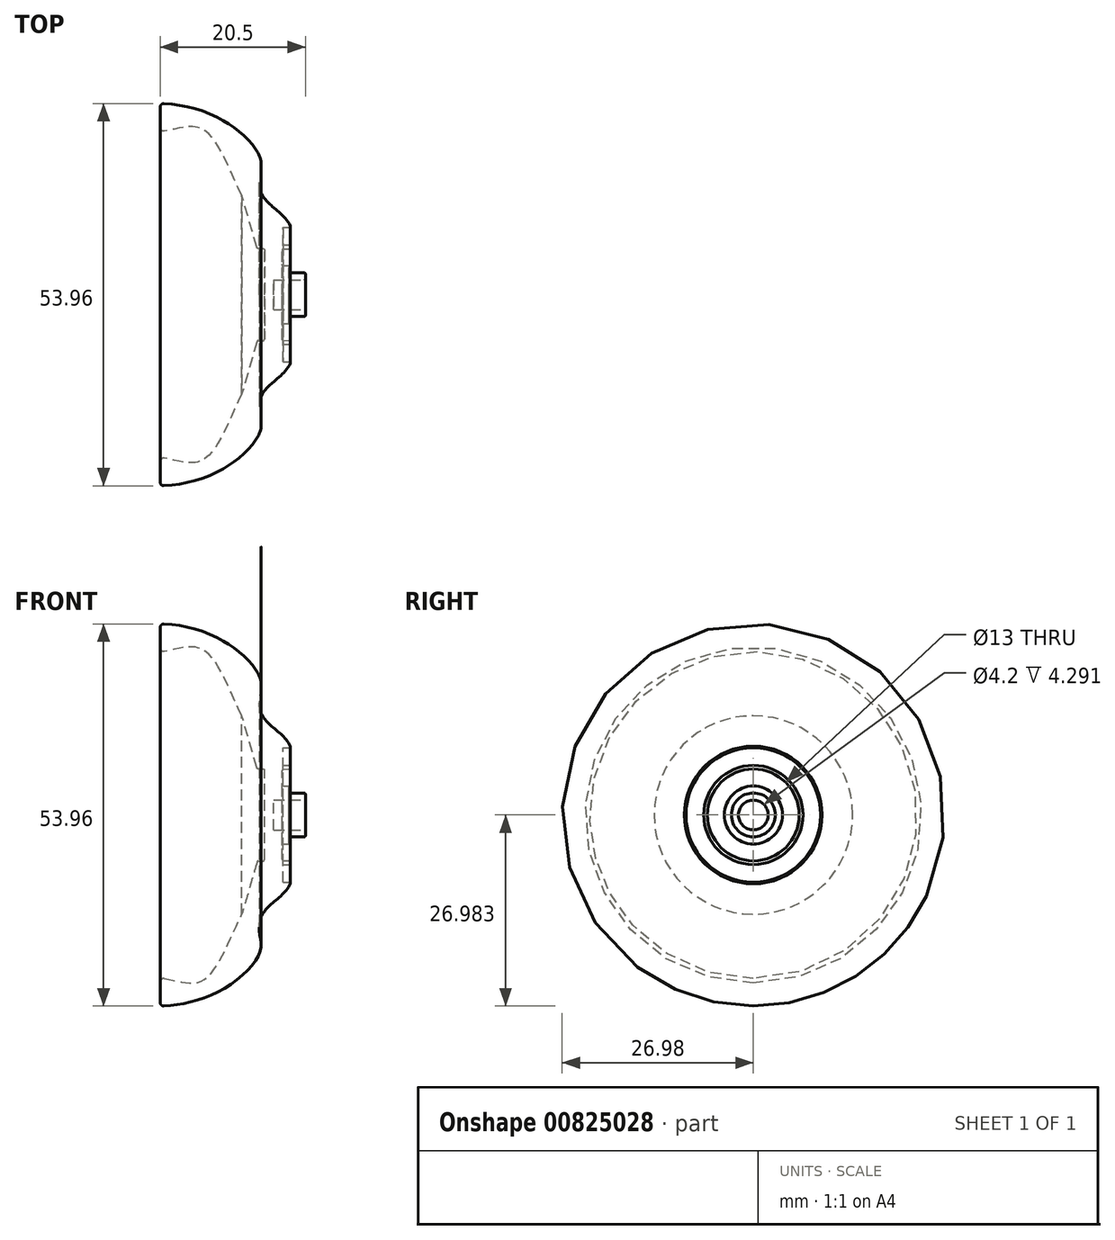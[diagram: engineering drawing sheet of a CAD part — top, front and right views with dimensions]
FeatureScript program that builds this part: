
annotation { "Feature Type Name" : "Feature", "Feature Type Description" : "" }
export const myFeature = defineFeature(function(context is Context, id is Id, definition is map)
    precondition{}
    {
        {
            var Q0;
            Q0=qCreatedBy(makeId("Front.planeOp"),FACE);
            var sketch = newSketch(context, id + "F0", { "sketchPlane" : qUnion([Q0])});
            skPoint(sketch, "E0", {"position": v(100.34, -4.5) * mm});
            skLineSegment(sketch, "E1", {"start": v(103.46, -7.12) * mm, "end": v(103.46, -6.52) * mm});
            skLineSegment(sketch, "E2", {"start": v(103.26, -6.32) * mm, "end": v(101.16, -6.32) * mm});
            skLineSegment(sketch, "E3", {"start": v(101.16, -6.32) * mm, "end": v(101.16, -5.52) * mm});
            skLineSegment(sketch, "E4", {"start": v(100.96, -5.32) * mm, "end": v(100.36, -5.32) * mm});
            skLineSegment(sketch, "E5", {"start": v(100.16, -5.12) * mm, "end": v(100.16, -3.16) * mm});
            skLineSegment(sketch, "E6", {"start": v(100.35, -2.96) * mm, "end": v(101.3, -2.94) * mm});
            skLineSegment(sketch, "E7", {"start": v(101.3, -2.94) * mm, "end": v(101.3, -2.42) * mm});
            skLineSegment(sketch, "E8", {"start": v(101.3, -2.42) * mm, "end": v(100.3, -2.42) * mm});
            skLineSegment(sketch, "E9", {"start": v(100.3, -2.42) * mm, "end": v(100.3, 0.08) * mm});
            skLineSegment(sketch, "E10", {"start": v(100.3, 0.08) * mm, "end": v(101.1, 0.08) * mm});
            skPoint(sketch, "E11.startSnap0", {"position": v(102.3, -6.32) * mm});
            skLineSegment(sketch, "E12", {"start": v(103.46, -9.42) * mm, "end": v(102.18, -9.42) * mm});
            skLineSegment(sketch, "E13", {"start": v(103.46, -9.42) * mm, "end": v(82.96, -9.42) * mm});
            skPoint(sketch, "E14.visualSharp", {"position": v(103.46, -7.32) * mm});
            skArc(sketch, "E14.filletArc", {"start": v(103.26, -7.32) * mm, "mid": v(103.4, -7.26) * mm, "end": v(103.46, -7.12) * mm});
            skPoint(sketch, "E15.visualSharp", {"position": v(103.46, -6.32) * mm});
            skArc(sketch, "E15.filletArc", {"start": v(103.46, -6.52) * mm, "mid": v(103.4, -6.38) * mm, "end": v(103.26, -6.32) * mm});
            skPoint(sketch, "E16.visualSharp", {"position": v(101.16, -5.32) * mm});
            skArc(sketch, "E16.filletArc", {"start": v(101.16, -5.52) * mm, "mid": v(101.1, -5.38) * mm, "end": v(100.96, -5.32) * mm});
            skPoint(sketch, "E17.visualSharp", {"position": v(100.16, -5.32) * mm});
            skArc(sketch, "E17.filletArc", {"start": v(100.16, -5.12) * mm, "mid": v(100.21, -5.26) * mm, "end": v(100.36, -5.32) * mm});
            skPoint(sketch, "E18.visualSharp", {"position": v(100.16, -2.97) * mm});
            skArc(sketch, "E18.filletArc", {"start": v(100.35, -2.96) * mm, "mid": v(100.21, -3.02) * mm, "end": v(100.16, -3.16) * mm});
            skPoint(sketch, "E19.visualSharp", {"position": v(101.3, 0.08) * mm});
            skArc(sketch, "E19.filletArc", {"start": v(101.1, 0.08) * mm, "mid": v(101.24, 0.15) * mm, "end": v(101.3, 0.3) * mm});
            skLineSegment(sketch, "E20", {"start": v(103.46, -9.42) * mm, "end": v(98.96, -9.42) * mm});
            skLineSegment(sketch, "E21", {"start": v(82.96, -9.42) * mm, "end": v(82.96, 17.58) * mm});
            skFitSpline(sketch, "E22", {"points": [v(82.96, 17.58) * mm, v(91.4, 15.4) * mm, v(97.04, 9.93) * mm, v(96.94, 6.98) * mm, v(97.74, 4.07) * mm, v(101.3, 0.3) * mm], "startDerivative": vector(30.11, -0.93) * mm, "endDerivative": vector(8.42, -22.03) * mm});
            skLineSegment(sketch, "E23", {"start": v(82.96, 17.06) * mm, "end": v(82.96, 14.16) * mm});
            skLineSegment(sketch, "E24", {"start": v(98.96, -9.42) * mm, "end": v(98.96, -7.32) * mm});
            skLineSegment(sketch, "E25", {"start": v(103.26, -7.32) * mm, "end": v(98.96, -7.32) * mm});
            skLineSegment(sketch, "E26", {"start": v(98.96, -9.42) * mm, "end": v(97.66, -9.42) * mm});
            skLineSegment(sketch, "E27", {"start": v(97.66, -9.42) * mm, "end": v(97.66, -3.12) * mm});
            skFitSpline(sketch, "E28", {"points": [v(82.96, 13.58) * mm, v(88.78, 14.01) * mm, v(94.49, 4.6) * mm], "startDerivative": vector(14.05, 1.46) * mm, "endDerivative": vector(10.13, -20.3) * mm});
            skArc(sketch, "E29.filletArc", {"start": v(83.5, 17.56) * mm, "mid": v(83.12, 17.42) * mm, "end": v(82.96, 17.06) * mm});
            skLineSegment(sketch, "E30", {"start": v(97.46, -2.92) * mm, "end": v(96.81, -2.92) * mm});
            skLineSegment(sketch, "E31", {"start": v(96.62, -2.77) * mm, "end": v(94.49, 4.6) * mm});
            skArc(sketch, "E32.filletArc", {"start": v(82.96, 14.16) * mm, "mid": v(83.14, 13.77) * mm, "end": v(83.55, 13.66) * mm});
            skPoint(sketch, "E33.visualSharp", {"position": v(97.66, -2.92) * mm});
            skArc(sketch, "E33.filletArc", {"start": v(97.66, -3.12) * mm, "mid": v(97.6, -2.98) * mm, "end": v(97.46, -2.92) * mm});
            skPoint(sketch, "E34.visualSharp", {"position": v(96.66, -2.92) * mm});
            skArc(sketch, "E34.filletArc", {"start": v(96.62, -2.77) * mm, "mid": v(96.7, -2.88) * mm, "end": v(96.81, -2.92) * mm});
            skSolve(sketch);
        }
        {
            var Q0;
            Q0=makeQuery(id+"F0.imprint","IMPRINT",FACE,{"disambiguationData":[TD([[makeQuery(id+"F0.imprint","IMPRINT",EDGE,{"derivedFrom":sQuery(id+"F0.wireOp",EDGE,"E1")}),1.0]])]});
            var Q1;
            Q1=sQuery(id+"F0.wireOp",EDGE,"E13");
            revolve(context, id + "F1", {"surfaceOperationType" : NewSurfaceOperationType.NEW, "entities" : qUnion([Q0]), "axis" : qUnion([Q1]), "revolveType" : RevolveType.FULL});
        }
    });
